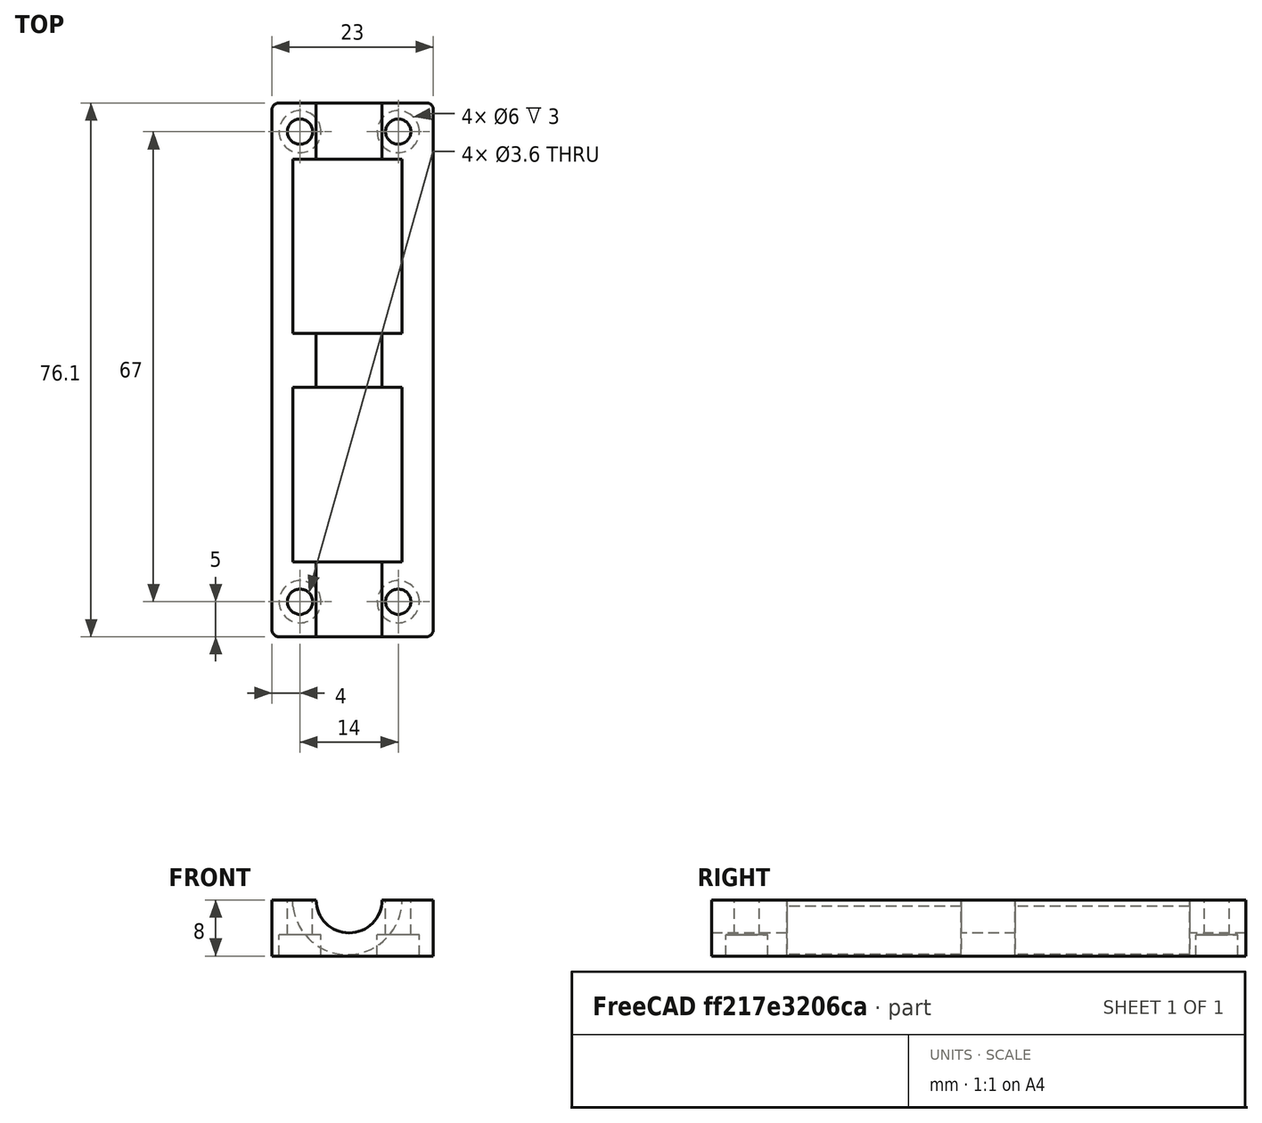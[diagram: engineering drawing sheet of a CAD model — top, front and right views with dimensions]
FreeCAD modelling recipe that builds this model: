
FCSTD DOCUMENT  (FreeCAD 0.16R6706 (Git))
Label: Carcasa 1 5.0
License: All rights reserved
LicenseURL: http://en.wikipedia.org/wiki/All_rights_reserved
objects: Part::Cut×6, Part::Cylinder×5, Part::Feature×1, Part::Fillet×1, Part::Prism×1
note: 14 computed .brp shape members not serialized (recipe doc carries the construction recipe); baked Part::Feature solids carry a one-line shape summary decoded from their .brp

FEATURE [Part::Cylinder] Cylinder049
  Angle = 360
  Height = 100
  Placement = pos=(88,79,0) rot=(1,0,0;1.5708rad)
  Radius = 4.7
FEATURE [Part::Feature] Fusion002001  label="Fusion004"
  shape: bbox 23 x 76.1 x 8 mm, 26 faces (baked)
FEATURE [Part::Fillet] Fillet003003  label="Carcasa 1'"
  Base = -> Fusion002001
  Edges = 2 edges r=1: [Edge61,Edge63]
FEATURE [Part::Cylinder] Cylinder035  label="Cilindro020"
  Angle = 360
  Height = 10
  Placement = pos=(81,72,-15) rot=(0,0,1;0rad)
  Radius = 3
FEATURE [Part::Cylinder] Cylinder036  label="Cilindro021"
  Angle = 360
  Height = 20
  Placement = pos=(81,72,-10) rot=(0,0,1;0rad)
  Radius = 1.8
FEATURE [Part::Cut] Cut010035003013
  Base = -> Fillet003003
  Tool = -> Cylinder035
FEATURE [Part::Cut] Cut010035003014  label="Carcasa 1''"
  Base = -> Cut010035003013
  Tool = -> Cylinder036
FEATURE [Part::Prism] Prism005  label="Prisma005"
  Circumradius = 3.7
  Height = 10
  Placement = pos=(81,5,5) rot=(0,0,1;0rad)
  Polygon = 6
FEATURE [Part::Cylinder] Cylinder038  label="Cilindro023"
  Angle = 360
  Height = 20
  Placement = pos=(81,5,-10) rot=(0,0,1;0rad)
  Radius = 1.8
FEATURE [Part::Cut] Cut010035003017
  Base = -> Cut010035003014
  Tool = -> Prism005
FEATURE [Part::Cut] Cut010035003018  label="Carcasa 1'''"
  Base = -> Cut010035003017
  Tool = -> Cylinder038
FEATURE [Part::Cylinder] Cylinder040  label="Cilindro025"
  Angle = 360
  Height = 10
  Placement = pos=(81,5,-15) rot=(0,0,1;0rad)
  Radius = 3
FEATURE [Part::Cut] Cut010035003020  label="Carcasa 1 V"
  Base = -> Cut010035003018
  Tool = -> Cylinder040
FEATURE [Part::Cut] Cut010035003031  label="Carcasa 1 VI"
  Base = -> Cut010035003020
  Tool = -> Cylinder049
